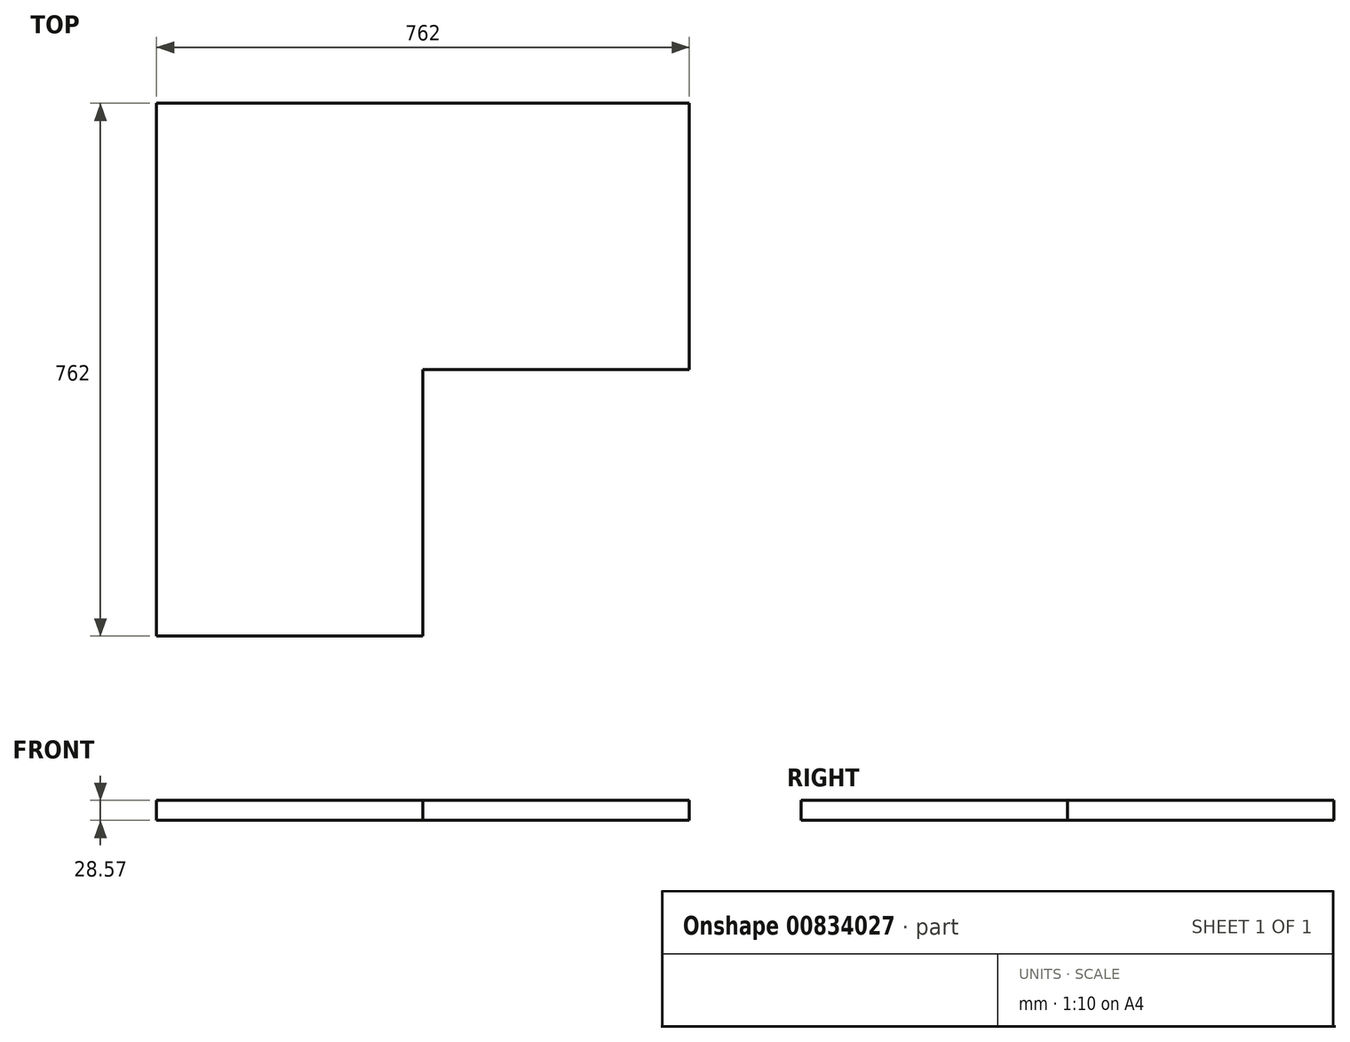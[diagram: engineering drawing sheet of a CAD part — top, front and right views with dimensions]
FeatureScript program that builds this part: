
annotation { "Feature Type Name" : "Feature", "Feature Type Description" : "" }
export const myFeature = defineFeature(function(context is Context, id is Id, definition is map)
    precondition{}
    {
        {
            var Q0;
            Q0=qCreatedBy(makeId("Top.planeOp"),FACE);
            var sketch = newSketch(context, id + "F0", { "sketchPlane" : qUnion([Q0])});
            skLineSegment(sketch, "E0.bottom", {"start": v(381, 381) * mm, "end": v(-381, 381) * mm});
            skLineSegment(sketch, "E0.top", {"start": v(381, -381) * mm, "end": v(-381, -381) * mm});
            skLineSegment(sketch, "E0.left", {"start": v(381, 381) * mm, "end": v(381, -381) * mm});
            skLineSegment(sketch, "E0.right", {"start": v(-381, 381) * mm, "end": v(-381, -381) * mm});
            skPoint(sketch, "E0.middle", {"position": v(0, 0) * mm});
            skLineSegment(sketch, "E1", {"start": v(0, 0) * mm, "end": v(381, 0) * mm});
            skLineSegment(sketch, "E2", {"start": v(0, 0) * mm, "end": v(0, -381) * mm});
            skSolve(sketch);
        }
        {
            var Q0;
            {var subQ1=sQuery(id+"F0.wireOp",EDGE,"E0.bottom");Q0=makeQuery(id+"F0.imprint","IMPRINT",FACE,{"disambiguationData":[TD([[makeQuery(id+"F0.imprint","IMPRINT",EDGE,{"derivedFrom":subQ1}),1.0]])]});}
            extrude(context, id + "F1", {"entities" : qUnion([Q0]), "depth" : 28.57 * mm, "offsetDistance" : 25.4 * mm});
        }
    });
